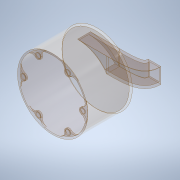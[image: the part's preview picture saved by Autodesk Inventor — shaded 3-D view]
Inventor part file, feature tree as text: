
AUTODESK INVENTOR PART (.ipt)
format: ipt  version: 2020 (Build 240168000, 168)  size: 367,104 bytes
history: native  units: in
note: dims shown in document units (in); Inventor stores cm internally (conversion verified against a paired STEP export)
features: sketch x13, extrude x10, projected_geometry x5, plane x2, shell x1, sweep x1, hole x1
ambient origin geometry x8: Origin, YZ Plane, XZ Plane, XY Plane, X Axis, Y Axis, Z Axis, Center Point
bodies: Solid1 (feature_tree)
feature tree (33):
  extrude  "Extrusion1"  Depth=3.1496in TaperAngle=0.0deg
  shell  "Shell1"  Thickness=0.1181in
  extrude  "Extrusion2"  Depth=3.1496in TaperAngle=0.0deg
  extrude  "Extrusion3"  Depth=1.5748in
  plane  "Work Plane1"
  extrude  "Extrusion4"  TaperAngle=120.0deg  [1 undecoded]
  extrude  "Extrusion5"  Depth=0.378in
  plane  "Work Plane4"
  sweep  "Sweep2"
  extrude  "Extrusion6"  [1 undecoded]
  hole  "Hole1"  [1 undecoded]
  extrude  "Extrusion9"  Depth=0.1181in TaperAngle=0.0deg
  extrude  "Extrusion10"  Depth=0.0591in
  extrude  "Extrusion11"  Depth=0.0591in
  extrude  "Extrusion12"  Depth=0.0591in
  sketch  "Sketch1"  dims[d1=5.3543in d2=3.1496in d3=0.0in d4=0.1181in]
  sketch  "Sketch2"  dims[d5=2.5197in d6=3.1496in d7=0.0in]
  sketch  "Sketch3"  dims[d8=0.378in d9=1.5748in]
  projected_geometry  "Projected Loop1"
  sketch  "Sketch4"  dims[d10=120.0deg d11=120.0deg]
  sketch  "Sketch6"  dims[d12=0.378in d13=0.378in]
  projected_geometry  "Projected Loop3"
  sketch  "Sketch9"  dims[d14=1.5748in d15=1.5748in]
  projected_geometry  "Projected Loop4"
  sketch  "Sketch10"  dims[d16=0.06in d17=0.0in d18=-1.7717in]
  sketch  "Sketch11"  dims[d24=1.1811in d25=0.9843in d26=0.0in]
  projected_geometry  "Projected Loop5"
  sketch  "Sketch14"  dims[d27=0.1181in d28=2.2201in d29=0.0in]
  sketch  "Sketch16"  dims[d37=0.0in d38=0.0in d39=0.0591in]
  sketch  "Sketch17"  dims[d40=0.0591in d41=0.0591in]
  sketch  "Sketch18"  dims[d42=0.0591in d43=0.0591in]
  projected_geometry  "Projected Loop7"
  sketch  "Sketch19"  dims[d44=0.0591in d45=0.0591in d46=0.9843in d47=0.9843in d48=0.9843in d49=0.9843in d50=0.9843in d51=0.9843in d52=0.0591in d53=0.0in d98=0.2362in d99=1.6142in d100=1.1811in d102=360.0deg d104=0.2362in d105=0.2362in d106=0.1575in d107=0.0787in d108=90.0deg d109=0.315in d110=0.8108in d111=0.1181in d112=0.0in d113=2.7559in d114=1.378in d115=1.378in d116=0.1181in d117=0.0in d118=0.378in d119=2.2638in d120=0.0591in d121=0.7874in d122=0.7874in d123=2.3622in d125=360.0deg d127=0.1181in d128=0.0in d129=0.378in d130=2.2638in d131=2.3622in d133=360.0deg d135=0.06in d136=0.0in]
note: 3 required parameter values undecoded (feature->parameter linkage not recoverable at this tier; creation-order binding heuristic only, values carry confidence <= 0.55)
